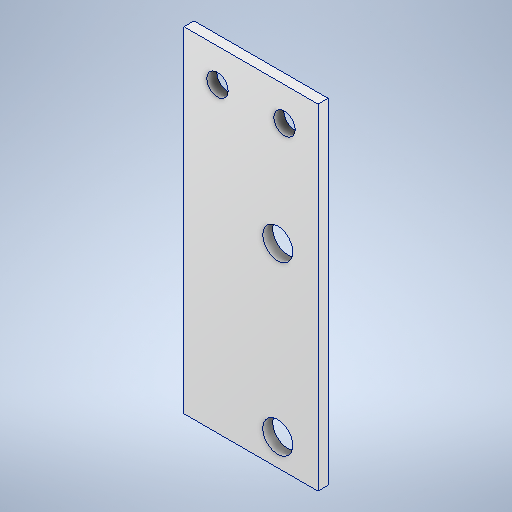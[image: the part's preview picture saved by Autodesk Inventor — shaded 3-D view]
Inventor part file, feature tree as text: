
AUTODESK INVENTOR PART (.ipt)
format: ipt  version: 2025 (Build 290162000, 162)  size: 272,384 bytes
history: native  units: mm
features: sketch x3, hole x2, other x1, extrude x1, projected_geometry x1
ambient origin geometry x8: Origin, YZ Plane, XZ Plane, XY Plane, X Axis, Y Axis, Z Axis, Center Point
bodies: Body1 (feature_tree)
feature tree (8):
  other  "Těleso1"
  extrude  "Vysunutí1"  Depth=50.0mm
  hole  "Díra1"  [1 undecoded]
  hole  "Díra2"  [1 undecoded]
  sketch  "Náčrt1"
  sketch  "Náčrt2"
  sketch  "Náčrt3"
  projected_geometry  "Promítnutá smyčka1"
note: 2 required parameter values undecoded (feature->parameter linkage not recoverable at this tier; creation-order binding heuristic only, values carry confidence <= 0.55)
